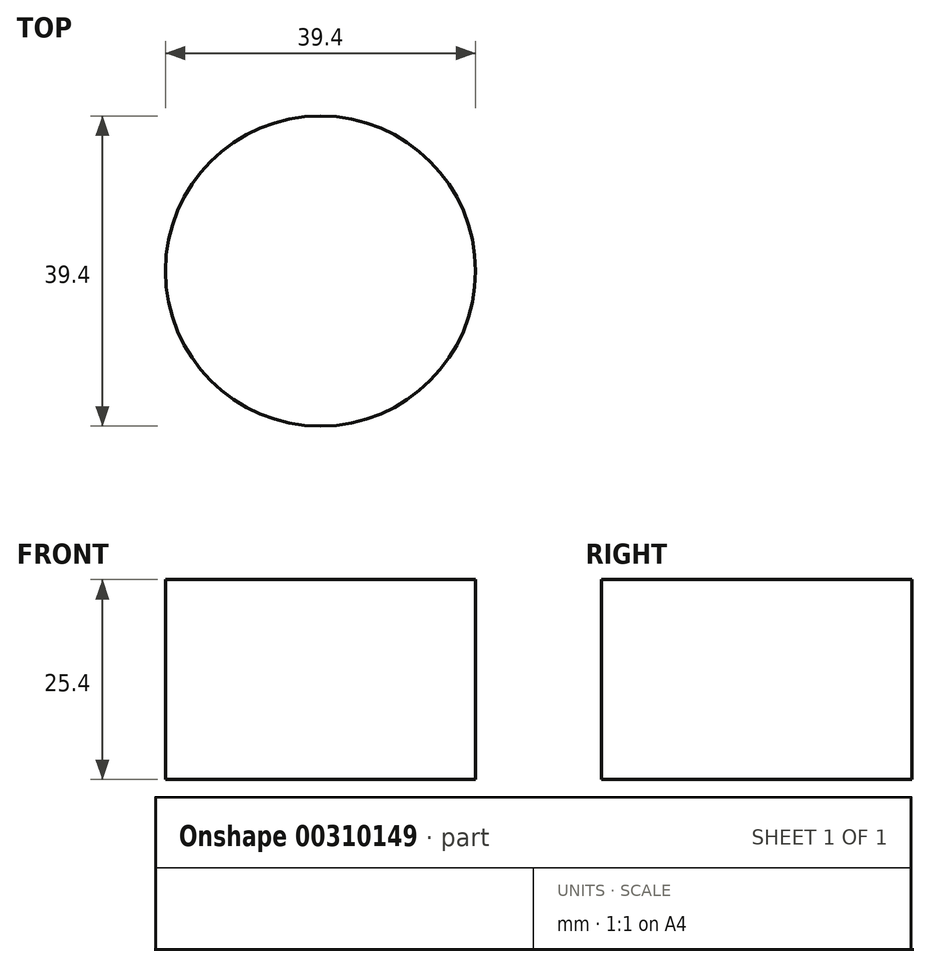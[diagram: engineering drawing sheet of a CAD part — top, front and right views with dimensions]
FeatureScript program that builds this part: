
annotation { "Feature Type Name" : "Feature", "Feature Type Description" : "" }
export const myFeature = defineFeature(function(context is Context, id is Id, definition is map)
    precondition{}
    {
        {
            var Q0;
            Q0=qCreatedBy(makeId("Top.planeOp"),FACE);
            var sketch = newSketch(context, id + "F0", { "sketchPlane" : qUnion([Q0])});
            skCircle(sketch, "E0", {"center": v(24.85, 38.7) * mm, "radius": 19.7 * mm});
            skSolve(sketch);
        }
        {
            var Q0;
            Q0 = qSketchRegion(id + "F0", true);
            extrude(context, id + "F1", {"entities" : qUnion([Q0]), "depth" : 25.4 * mm});
        }
    });
